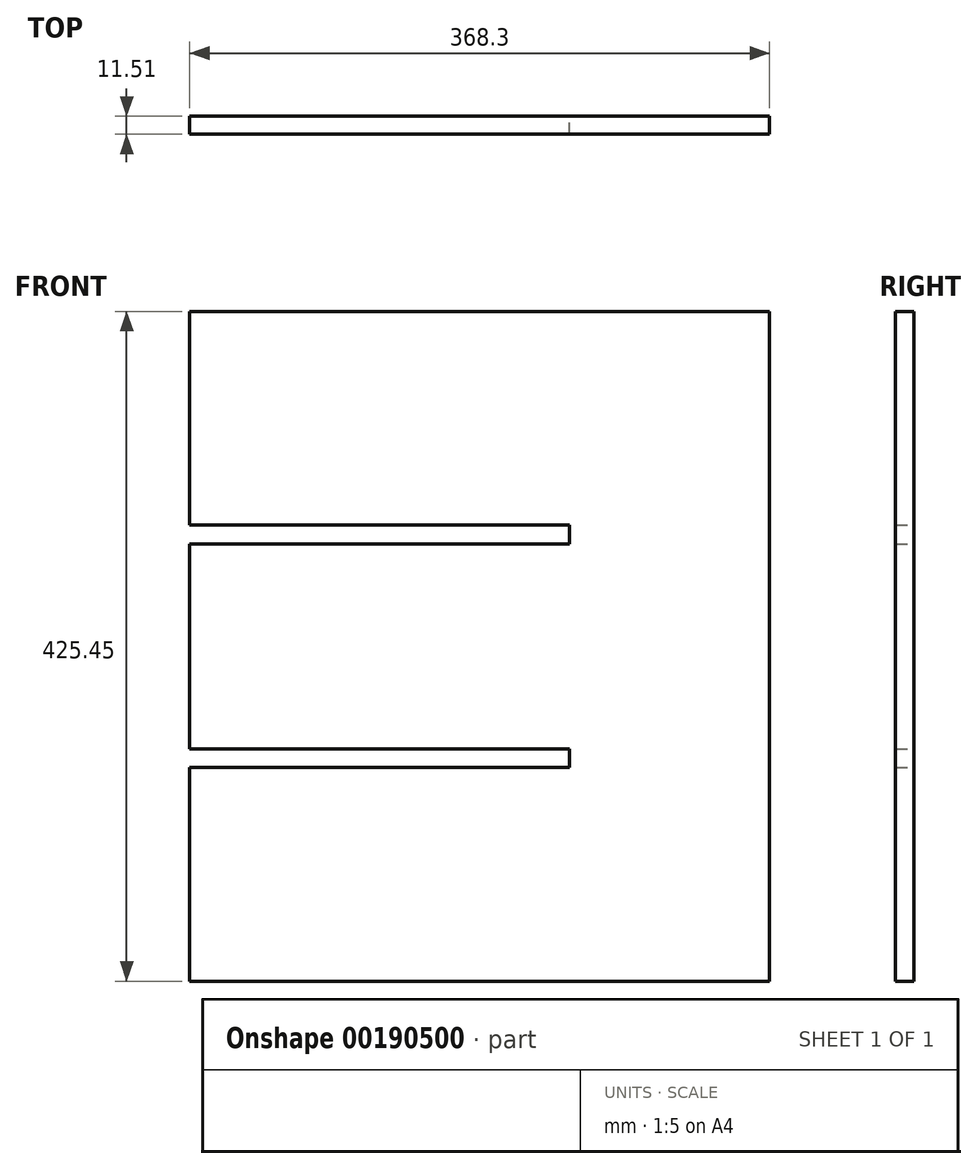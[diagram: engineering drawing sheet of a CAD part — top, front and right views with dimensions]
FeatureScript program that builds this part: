
annotation { "Feature Type Name" : "Feature", "Feature Type Description" : "" }
export const myFeature = defineFeature(function(context is Context, id is Id, definition is map)
    precondition{}
    {
        {
            var Q0;
            Q0=qCreatedBy(makeId("Front.planeOp"),FACE);
            var sketch = newSketch(context, id + "F0", { "sketchPlane" : qUnion([Q0])});
            skLineSegment(sketch, "E0.bottom", {"start": v(-168.85, 221.94) * mm, "end": v(199.45, 221.94) * mm});
            skLineSegment(sketch, "E0.top", {"start": v(-168.85, -203.51) * mm, "end": v(199.45, -203.51) * mm});
            skLineSegment(sketch, "E0.left", {"start": v(-168.85, 221.94) * mm, "end": v(-168.85, 86.2) * mm});
            skLineSegment(sketch, "E0.right", {"start": v(199.45, 221.94) * mm, "end": v(199.45, -203.51) * mm});
            skLineSegment(sketch, "E1", {"start": v(-168.85, 80.25) * mm, "end": v(199.45, 80.25) * mm, "construction": true});
            skLineSegment(sketch, "E2", {"start": v(-168.85, -61.83) * mm, "end": v(199.45, -61.83) * mm, "construction": true});
            skLineSegment(sketch, "E3", {"start": v(-168.85, 86.2) * mm, "end": v(72.45, 86.2) * mm});
            skLineSegment(sketch, "E4", {"start": v(72.45, 86.2) * mm, "end": v(72.45, 80.25) * mm});
            skLineSegment(sketch, "E5.MirrorCS", {"start": v(-168.85, 74.3) * mm, "end": v(72.45, 74.3) * mm});
            skLineSegment(sketch, "E6.MirrorCS", {"start": v(72.45, 74.3) * mm, "end": v(72.45, 80.25) * mm});
            skLineSegment(sketch, "E7", {"start": v(-168.85, -55.88) * mm, "end": v(72.45, -55.88) * mm});
            skLineSegment(sketch, "E8", {"start": v(72.45, -55.88) * mm, "end": v(72.45, -61.83) * mm});
            skLineSegment(sketch, "E9.MirrorCS", {"start": v(-168.85, -67.78) * mm, "end": v(72.45, -67.78) * mm});
            skLineSegment(sketch, "E10.MirrorCS", {"start": v(72.45, -67.78) * mm, "end": v(72.45, -61.83) * mm});
            skLineSegment(sketch, "E11.trimOffspring", {"start": v(-168.85, 74.3) * mm, "end": v(-168.85, -55.88) * mm});
            skLineSegment(sketch, "E12.trimOffspring", {"start": v(-168.85, -67.78) * mm, "end": v(-168.85, -203.51) * mm});
            skSolve(sketch);
        }
        {
            var Q0;
            Q0 = qSketchRegion(id + "F0", true);
            extrude(context, id + "F1", {"entities" : qUnion([Q0]), "depth" : 11.5 * mm});
        }
    });
